# Revit family: NLRS_57_AIR_UN_induction-unit-okni450_LT_sacs
name_source: partatom
category: Mechanical Equipment
units: mm (PartAtom-declared; Revit-internal decimal feet)

## family parameters
Always vertical = Yes
Classification = None
Cut with Voids When Loaded = No
OmniClass Number = 23.75.00.00
OmniClass Title = Climate Control (HVAC)
Part Type = Normal
Room Calculation Point = No
Round Connector Dimension = Use Diameter
Shared = No
Work Plane-Based = No

## types (5) — shared parameters
Assembly Code = 57.00
Description = Induction unit for use in modular ceilings, Type OKNI 450
FireRating = 00
IfcDescription = Induction unit for use in modular ceilings, Type OKNI 450
IfcExportAs = IfcAirTerminalType
IfcExportType = DIFFUSER
LoadBearing = No
Manufacturer = Solid Air Climate Solutions
Model = Solid Air Induction Unit OKNI 450
NLRS_C_content_datum_uitgifte = 30-05-2023
NLRS_C_content_provider = Solid Air Climate Solutions
NLRS_C_content_versie = 3.20.01
SACS_Offset2 = 35 mm  [stored 0.114829 ft]
SACS_Plenum_Material = Sendzimir verzinkt
SACS_Real_Width = 445 mm  [stored 1.45997 ft]
SACS_Type_Toggle = No
Type Comments = Do not mirror the model!
URL = https://solid-air.nl
zero-valued in all types: Default Elevation

## per-type parameters (varying)
| type | SACS_Base_Index | SACS_Length_STD | SACS_Length_X2 | SACS_Logo_X | SACS_Offset1 | SACS_Plenum_L | SACS_Plenum_Offset |
| 450-1200 | 1 | 1195 mm  [stored 3.9206 ft] | 1090 mm  [stored 3.57612 ft] | 465 mm  [stored 1.52559 ft] | 35 mm  [stored 0.114829 ft] | 980 mm  [stored 3.21522 ft] | 555 mm  [stored 1.82087 ft] |
| 450-1500 | 2 | 1495 mm | 1390 mm  [stored 4.56037 ft] | 615 mm  [stored 2.01772 ft] | 35 mm  [stored 0.114829 ft] | 1280 mm  [stored 4.19948 ft] | 705 mm  [stored 2.31299 ft] |
| 450-1800 | 3 | 1795 mm | 1640 mm  [stored 5.38058 ft] | 730 mm  [stored 2.39501 ft] | 55 mm  [stored 0.180446 ft] | 1510 mm  [stored 4.95407 ft] | 840 mm  [stored 2.75591 ft] |
| 450-2400 | 4 | 2395 mm  [stored 7.85761 ft] | 2240 mm  [stored 7.34908 ft] | 1030 mm  [stored 3.37927 ft] | 55 mm  [stored 0.180446 ft] | 2110 mm  [stored 6.92257 ft] | 1140 mm  [stored 3.74016 ft] |
| 450-3000 | 5 | 2995 mm  [stored 9.82612 ft] | 2840 mm | 1330 mm  [stored 4.36352 ft] | 55 mm  [stored 0.180446 ft] | 2710 mm  [stored 8.89108 ft] | 1440 mm  [stored 4.72441 ft] |

note: [stored X ft] marks values corroborated as IEEE doubles in the binary element streams (Revit-internal decimal feet)

## geometry (parser evidence)
native form markers: Sweep x10
no freeform markers — native parametric forms only
